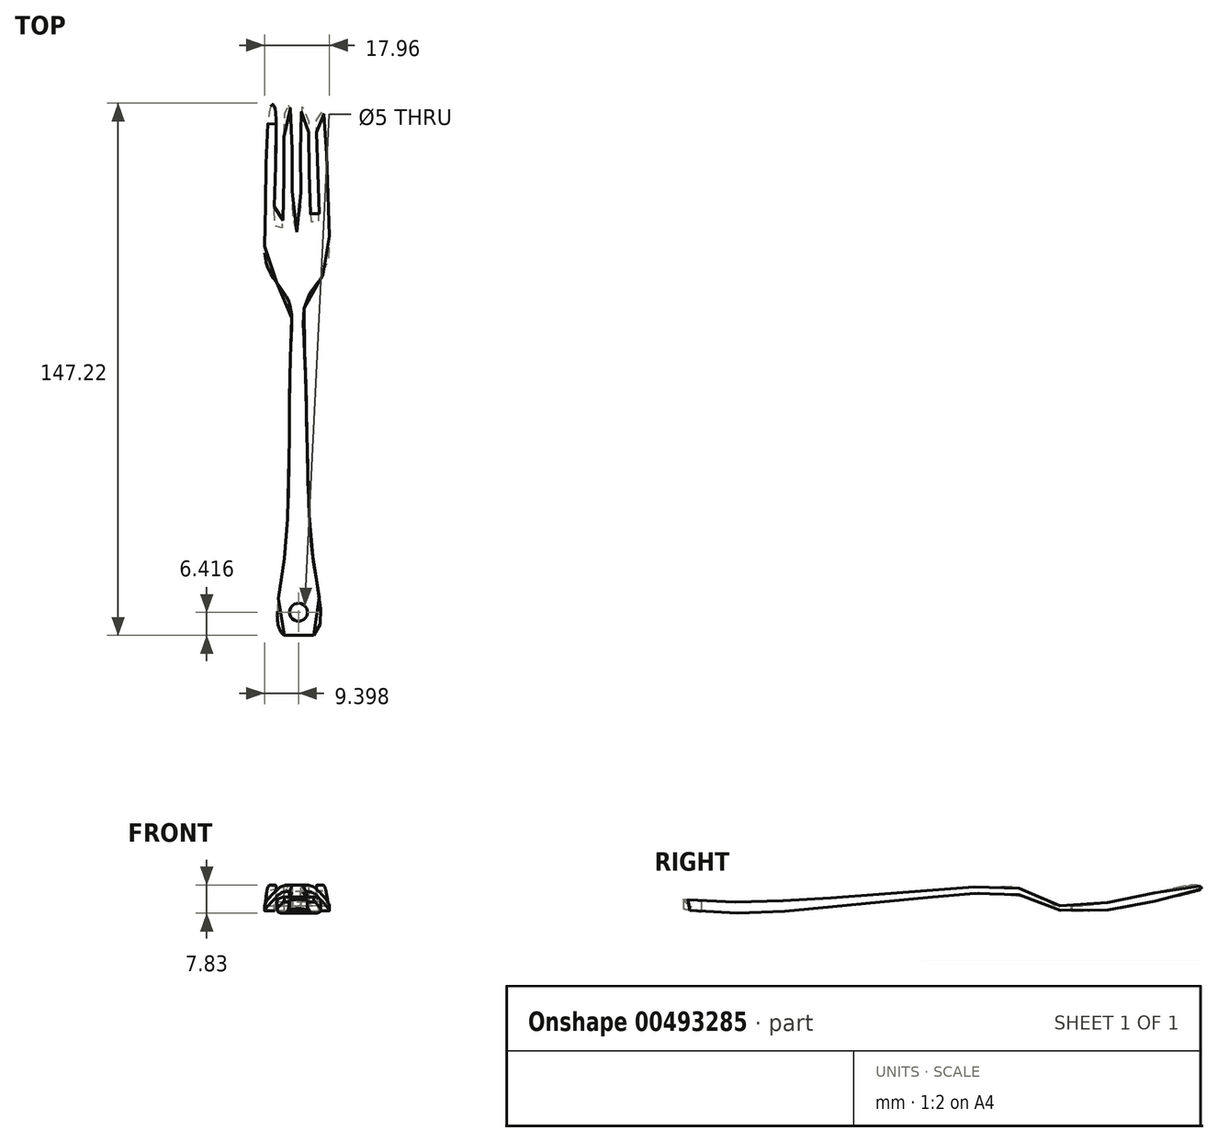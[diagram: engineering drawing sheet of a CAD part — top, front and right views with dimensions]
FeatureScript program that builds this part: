
annotation { "Feature Type Name" : "Feature", "Feature Type Description" : "" }
export const myFeature = defineFeature(function(context is Context, id is Id, definition is map)
    precondition{}
    {
        {
            var Q0;
            Q0=qCreatedBy(makeId("Top.planeOp"),FACE);
            var sketch = newSketch(context, id + "F0", { "sketchPlane" : qUnion([Q0])});
            skLineSegment(sketch, "E0.bottom", {"start": v(50, -90) * mm, "end": v(-50, -90) * mm});
            skLineSegment(sketch, "E0.top", {"start": v(50, 90) * mm, "end": v(-50, 90) * mm});
            skLineSegment(sketch, "E0.left", {"start": v(50, -90) * mm, "end": v(50, 90) * mm});
            skLineSegment(sketch, "E0.right", {"start": v(-50, -90) * mm, "end": v(-50, 90) * mm});
            skPoint(sketch, "E0.middle", {"position": v(0, 0) * mm});
            skSolve(sketch);
        }
        {
            var Q0;
            Q0=qSketchRegion(id+"F0",true);
            extrude(context, id + "F1", {"entities" : qUnion([Q0]), "depth" : 25 * mm});
        }
        {
            var Q0;
            Q0=makeQuery(id+"F1.opExtrude","CAP_FACE",FACE,{"disambiguationData":[OSD([sQuery(id+"F0.wireOp",EDGE,"E0.bottom"),sQuery(id+"F0.wireOp",EDGE,"E0.top"),sQuery(id+"F0.wireOp",EDGE,"E0.left"),sQuery(id+"F0.wireOp",EDGE,"E0.right")])],"isStart":false});
            var sketch = newSketch(context, id + "F2", { "sketchPlane" : qUnion([Q0])});
            skFitSpline(sketch, "E1", {"points": [v(2.1, 40.97) * mm, v(2.83, 41.82) * mm, v(3.55, 75.36) * mm, v(4.4, 76.58) * mm, v(5.13, 74.75) * mm, v(6.35, 41.7) * mm, v(7.2, 40.72) * mm, v(8.05, 42.19) * mm, v(7.68, 74.63) * mm, v(8.54, 76.34) * mm, v(9.55, 73.15) * mm, v(10.93, 43.26) * mm, v(9.9, 30.34) * mm, v(4.77, 22.25) * mm, v(4.22, 8.07) * mm, v(5.96, -44.04) * mm, v(8.34, -60.48) * mm, v(7.84, -69.45) * mm, v(2.73, -72.37) * mm], "startDerivative": vector(44.58, 9.27) * mm, "endDerivative": vector(-161.88, -49.21) * mm});
            skFitSpline(sketch, "E2.MirrorCS", {"points": [v(2.11, 40.97) * mm, v(1.37, 41.81) * mm, v(0.27, 75.34) * mm, v(-0.6, 76.55) * mm, v(-1.3, 74.72) * mm, v(-2.15, 41.65) * mm, v(-3, 40.66) * mm, v(-3.86, 42.12) * mm, v(-3.85, 74.57) * mm, v(-4.72, 76.27) * mm, v(-5.7, 73.06) * mm, v(-6.75, 43.16) * mm, v(-5.58, 30.26) * mm, v(-0.36, 22.23) * mm, v(0.35, 8.05) * mm, v(-0.81, -44.07) * mm, v(-3, -60.54) * mm, v(-2.41, -69.5) * mm, v(2.73, -72.37) * mm], "startDerivative": vector(-44.68, 8.78) * mm, "endDerivative": vector(162.42, -47.42) * mm});
            skSolve(sketch);
        }
        {
            var Q0;
            Q0=makeQuery(id+"F1.opExtrude","SWEPT_FACE",FACE,{"disambiguationData":[OSD([sQuery(id+"F0.wireOp",EDGE,"E0.right")])]});
            var sketch = newSketch(context, id + "F3", { "sketchPlane" : qUnion([Q0])});
            skFitSpline(sketch, "E3", {"points": [v(-76.13, 15.3) * mm, v(-63.25, 13.2) * mm, v(-34.36, 10.25) * mm, v(-25.9, 14.72) * mm, v(-19.48, 15.3) * mm, v(30.44, 11.62) * mm, v(57.85, 10.86) * mm, v(69.64, 11.93) * mm, v(70.43, 12.06) * mm, v(70.58, 11.17) * mm, v(66.8, 8.97) * mm, v(50.63, 7.67) * mm, v(25.05, 9.46) * mm, v(-23.1, 13.62) * mm, v(-26.36, 12.68) * mm, v(-31.63, 9.43) * mm, v(-38.43, 8.42) * mm, v(-47.59, 8.44) * mm, v(-57.48, 9.67) * mm, v(-74.94, 13.83) * mm, v(-76.64, 14.58) * mm, v(-76.13, 15.3) * mm]});
            skSolve(sketch);
        }
        {
            var Q0;
            Q0=qSketchRegion(id+"F3",true);
            extrude(context, id + "F4", {"entities" : qUnion([Q0]), "operationType" : NewBodyOperationType.INTERSECT, "oppositeDirection" : true, "depth" : 200 * mm});
        }
        {
            var Q0;
            Q0=qSketchRegion(id+"F2",true);
            extrude(context, id + "F5", {"entities" : qUnion([Q0]), "operationType" : NewBodyOperationType.INTERSECT, "oppositeDirection" : true, "depth" : 30 * mm});
        }
        {
            var Q0;
            Q0=qCreatedBy(makeId("Top.planeOp"),FACE);
            var sketch = newSketch(context, id + "F6", { "sketchPlane" : qUnion([Q0])});
            skLineSegment(sketch, "E4", {"start": v(-1.64, -70.6) * mm, "end": v(6.72, -70.6) * mm, "construction": true});
            skLineSegment(sketch, "E5", {"start": v(2.54, -70.6) * mm, "end": v(2.54, -64.21) * mm, "construction": true});
            skCircle(sketch, "E6", {"center": v(2.54, -64.21) * mm, "radius": 2.5 * mm});
            skSolve(sketch);
        }
        {
            var Q0;
            Q0=qSketchRegion(id+"F6",true);
            extrude(context, id + "F7", {"entities" : qUnion([Q0]), "operationType" : NewBodyOperationType.REMOVE, "depth" : 30.3 * mm});
        }
    });
